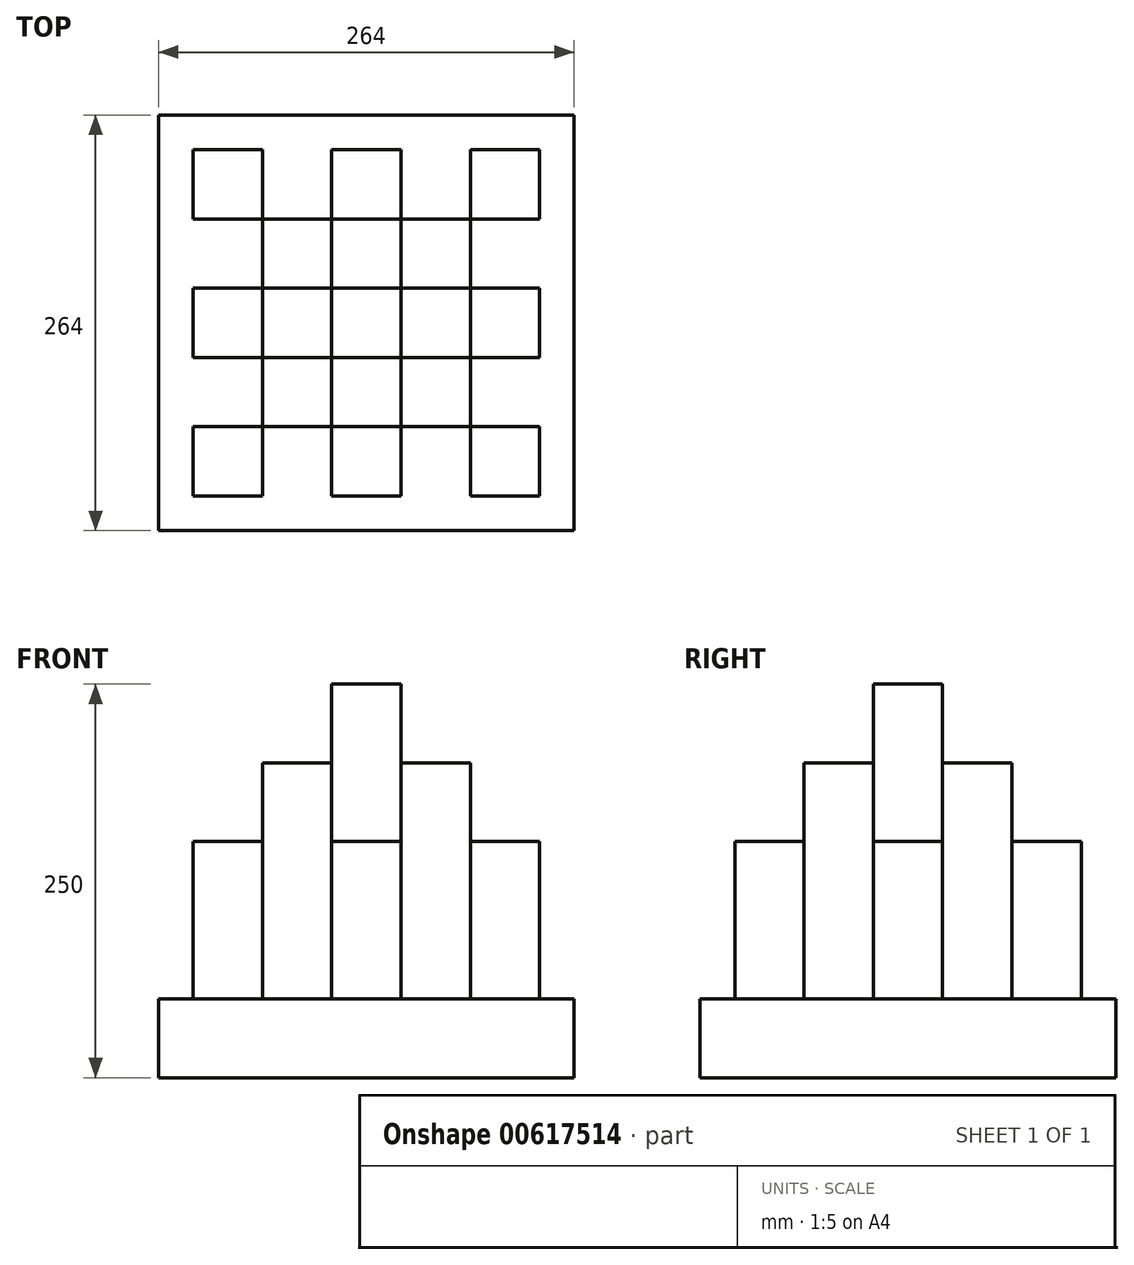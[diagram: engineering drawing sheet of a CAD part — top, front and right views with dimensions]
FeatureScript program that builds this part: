
annotation { "Feature Type Name" : "Feature", "Feature Type Description" : "" }
export const myFeature = defineFeature(function(context is Context, id is Id, definition is map)
    precondition{}
    {
        {
            var Q0;
            Q0=qCreatedBy(makeId("Top.planeOp"),FACE);
            var sketch = newSketch(context, id + "F0", { "sketchPlane" : qUnion([Q0])});
            skLineSegment(sketch, "E0.bottom", {"start": v(22, -22) * mm, "end": v(-22, -22) * mm});
            skLineSegment(sketch, "E0.top", {"start": v(22, 22) * mm, "end": v(-22, 22) * mm});
            skLineSegment(sketch, "E0.left", {"start": v(22, -22) * mm, "end": v(22, 22) * mm});
            skLineSegment(sketch, "E0.right", {"start": v(-22, -22) * mm, "end": v(-22, 22) * mm});
            skPoint(sketch, "E0.middle", {"position": v(0, 0) * mm});
            skLineSegment(sketch, "E1.bottom", {"start": v(-66, -22) * mm, "end": v(-110, -22) * mm});
            skLineSegment(sketch, "E1.top", {"start": v(-66, 22) * mm, "end": v(-110, 22) * mm});
            skLineSegment(sketch, "E1.left", {"start": v(-66, -22) * mm, "end": v(-66, 22) * mm});
            skLineSegment(sketch, "E1.right", {"start": v(-110, -22) * mm, "end": v(-110, 22) * mm});
            skPoint(sketch, "E1.middle", {"position": v(-88, 0) * mm});
            skPoint(sketch, "E1.middle.positionSnap0", {"position": v(-22, 0) * mm});
            skPoint(sketch, "E1.centerSnap0", {"position": v(-22, 0) * mm});
            skLineSegment(sketch, "E2.bottom", {"start": v(22, 66) * mm, "end": v(-22, 66) * mm});
            skLineSegment(sketch, "E2.top", {"start": v(22, 110) * mm, "end": v(-22, 110) * mm});
            skLineSegment(sketch, "E2.left", {"start": v(22, 66) * mm, "end": v(22, 110) * mm});
            skLineSegment(sketch, "E2.right", {"start": v(-22, 66) * mm, "end": v(-22, 110) * mm});
            skLineSegment(sketch, "E3.bottom", {"start": v(-66, 66) * mm, "end": v(-110, 66) * mm});
            skLineSegment(sketch, "E3.top", {"start": v(-66, 110) * mm, "end": v(-110, 110) * mm});
            skLineSegment(sketch, "E3.left", {"start": v(-66, 66) * mm, "end": v(-66, 110) * mm});
            skLineSegment(sketch, "E3.right", {"start": v(-110, 66) * mm, "end": v(-110, 110) * mm});
            skLineSegment(sketch, "E4.bottom", {"start": v(-132, 132) * mm, "end": v(132, 132) * mm});
            skLineSegment(sketch, "E4.top", {"start": v(-132, -132) * mm, "end": v(132, -132) * mm});
            skLineSegment(sketch, "E4.left", {"start": v(-132, 132) * mm, "end": v(-132, -132) * mm});
            skLineSegment(sketch, "E4.right", {"start": v(132, 132) * mm, "end": v(132, -132) * mm});
            skSolve(sketch);
        }
        {
            var Q0;
            Q0=makeQuery(id+"F0.imprint","IMPRINT",FACE,{"disambiguationData":[TD([[makeQuery(id+"F0.imprint","IMPRINT",EDGE,{"derivedFrom":sQuery(id+"F0.wireOp",EDGE,"E1.bottom")}),-1.0]])]});
            var Q1;
            Q1=makeQuery(id+"F0.imprint","IMPRINT",FACE,{"disambiguationData":[TD([[makeQuery(id+"F0.imprint","IMPRINT",EDGE,{"derivedFrom":sQuery(id+"F0.wireOp",EDGE,"E3.bottom")}),-1.0]])]});
            var Q2;
            Q2=makeQuery(id+"F0.imprint","IMPRINT",FACE,{"disambiguationData":[TD([[makeQuery(id+"F0.imprint","IMPRINT",EDGE,{"derivedFrom":sQuery(id+"F0.wireOp",EDGE,"E2.bottom")}),-1.0]])]});
            var Q3;
            Q3=makeQuery(id+"F0.imprint","IMPRINT",FACE,{"disambiguationData":[TD([[makeQuery(id+"F0.imprint","IMPRINT",EDGE,{"derivedFrom":sQuery(id+"F0.wireOp",EDGE,"E0.bottom")}),-1.0]])]});
            extrude(context, id + "F1", {"entities" : qUnion([Q0, Q1, Q2, Q3]), "depth" : 100 * mm, "offsetDistance" : 25 * mm});
        }
        {
            var Q0;
            Q0=makeQuery(id+"F1.opExtrude","SWEPT_BODY",BODY,{"disambiguationData":[OSD([sQuery(id+"F0.wireOp",EDGE,"E1.bottom"),sQuery(id+"F0.wireOp",EDGE,"E1.top"),sQuery(id+"F0.wireOp",EDGE,"E1.left"),sQuery(id+"F0.wireOp",EDGE,"E1.right")])]});
            var Q1;
            Q1=makeQuery(id+"F1.opExtrude","SWEPT_BODY",BODY,{"disambiguationData":[OSD([sQuery(id+"F0.wireOp",EDGE,"E3.bottom"),sQuery(id+"F0.wireOp",EDGE,"E3.top"),sQuery(id+"F0.wireOp",EDGE,"E3.left"),sQuery(id+"F0.wireOp",EDGE,"E3.right")])]});
            var Q2;
            Q2=qCreatedBy(makeId("Right.planeOp"),FACE);
            mirror(context, id + "F2", {"entities" : qUnion([Q0, Q1]), "mirrorPlane" : qUnion([Q2])});
        }
        {
            var Q0;
            Q0=makeQuery(id+"F1.opExtrude","SWEPT_BODY",BODY,{"disambiguationData":[OSD([sQuery(id+"F0.wireOp",EDGE,"E3.bottom"),sQuery(id+"F0.wireOp",EDGE,"E3.top"),sQuery(id+"F0.wireOp",EDGE,"E3.left"),sQuery(id+"F0.wireOp",EDGE,"E3.right")])]});
            var Q1;
            Q1=makeQuery(id+"F1.opExtrude","SWEPT_BODY",BODY,{"disambiguationData":[OSD([sQuery(id+"F0.wireOp",EDGE,"E2.bottom"),sQuery(id+"F0.wireOp",EDGE,"E2.top"),sQuery(id+"F0.wireOp",EDGE,"E2.left"),sQuery(id+"F0.wireOp",EDGE,"E2.right")])]});
            var Q2;
            Q2=makeQuery(id+"F2.opPattern","COPY",BODY,{"derivedFrom":makeQuery(id+"F1.opExtrude","SWEPT_BODY",BODY,{"disambiguationData":[OSD([sQuery(id+"F0.wireOp",EDGE,"E3.bottom"),sQuery(id+"F0.wireOp",EDGE,"E3.top"),sQuery(id+"F0.wireOp",EDGE,"E3.left"),sQuery(id+"F0.wireOp",EDGE,"E3.right")])]}),"instanceName":"1"});
            var Q3;
            Q3=qCreatedBy(makeId("Front.planeOp"),FACE);
            mirror(context, id + "F3", {"entities" : qUnion([Q0, Q1, Q2]), "mirrorPlane" : qUnion([Q3])});
        }
        {
            var Q0;
            Q0=makeQuery(id+"F0.imprint","IMPRINT",FACE,{"disambiguationData":[TD([[makeQuery(id+"F0.imprint","IMPRINT",EDGE,{"derivedFrom":sQuery(id+"F0.wireOp",EDGE,"E0.bottom")}),1.0]])]});
            var Q1;
            Q1=makeQuery(id+"F0.imprint","IMPRINT",FACE,{"disambiguationData":[TD([[makeQuery(id+"F0.imprint","IMPRINT",EDGE,{"derivedFrom":sQuery(id+"F0.wireOp",EDGE,"E1.bottom")}),-1.0]])]});
            var Q2;
            Q2=makeQuery(id+"F0.imprint","IMPRINT",FACE,{"disambiguationData":[TD([[makeQuery(id+"F0.imprint","IMPRINT",EDGE,{"derivedFrom":sQuery(id+"F0.wireOp",EDGE,"E0.bottom")}),-1.0]])]});
            var Q3;
            Q3=makeQuery(id+"F0.imprint","IMPRINT",FACE,{"disambiguationData":[TD([[makeQuery(id+"F0.imprint","IMPRINT",EDGE,{"derivedFrom":sQuery(id+"F0.wireOp",EDGE,"E3.bottom")}),-1.0]])]});
            var Q4;
            Q4=makeQuery(id+"F0.imprint","IMPRINT",FACE,{"disambiguationData":[TD([[makeQuery(id+"F0.imprint","IMPRINT",EDGE,{"derivedFrom":sQuery(id+"F0.wireOp",EDGE,"E2.bottom")}),-1.0]])]});
            var Q5;
            Q5=makeQuery(id+"F0.imprint","IMPRINT",FACE,{"disambiguationData":[TD([[makeQuery(id+"F0.imprint","IMPRINT",EDGE,{"derivedFrom":sQuery(id+"F0.wireOp",EDGE,"s8nrxy9o-eQNT-J21R-3rhY-hXZDEOxniQx1.bottom")}),-1.0]])]});
            var Q6;
            Q6=makeQuery(id+"F0.imprint","IMPRINT",FACE,{"disambiguationData":[TD([[makeQuery(id+"F0.imprint","IMPRINT",EDGE,{"derivedFrom":sQuery(id+"F0.wireOp",EDGE,"qjdVoqcM-cdFN-DcoX-eKo3-hN4eeX86174q.bottom")}),-1.0]])]});
            var Q7;
            Q7=makeQuery(id+"F0.imprint","IMPRINT",FACE,{"disambiguationData":[TD([[makeQuery(id+"F0.imprint","IMPRINT",EDGE,{"derivedFrom":sQuery(id+"F0.wireOp",EDGE,"QuOzhZ4j-HeuV-gT1i-nwIz-iXForqPxwVGl.bottom")}),-1.0]])]});
            var Q8;
            Q8=makeQuery(id+"F0.imprint","IMPRINT",FACE,{"disambiguationData":[TD([[makeQuery(id+"F0.imprint","IMPRINT",EDGE,{"derivedFrom":sQuery(id+"F0.wireOp",EDGE,"E0.top")}),-1.0]])]});
            var Q9;
            Q9=makeQuery(id+"F0.imprint","IMPRINT",FACE,{"disambiguationData":[TD([[makeQuery(id+"F0.imprint","IMPRINT",EDGE,{"derivedFrom":sQuery(id+"F0.wireOp",EDGE,"shoo1xml-Vqwe-dRvA-hi83-8JOpAzoyQhsb.bottom")}),-1.0]])]});
            var Q10;
            Q10=makeQuery(id+"F0.imprint","IMPRINT",FACE,{"disambiguationData":[TD([[makeQuery(id+"F0.imprint","IMPRINT",EDGE,{"derivedFrom":sQuery(id+"F0.wireOp",EDGE,"E0.right")}),1.0]])]});
            extrude(context, id + "F4", {"entities" : qUnion([Q0, Q1, Q2, Q3, Q4, Q5, Q6, Q7, Q8, Q9, Q10]), "oppositeDirection" : true, "depth" : 50 * mm, "offsetDistance" : 25 * mm});
        }
        {
            var Q0;
            Q0=makeQuery(id+"F4.opExtrude","CAP_FACE",FACE,{"disambiguationData":[OSD([sQuery(id+"F0.wireOp",EDGE,"E4.bottom"),sQuery(id+"F0.wireOp",EDGE,"E4.top"),sQuery(id+"F0.wireOp",EDGE,"E4.left"),sQuery(id+"F0.wireOp",EDGE,"E4.right")])],"isStart":true});
            var sketch = newSketch(context, id + "F5", { "sketchPlane" : qUnion([Q0])});
            skLineSegment(sketch, "E5.bottom", {"start": v(-66, 66) * mm, "end": v(-22, 66) * mm});
            skLineSegment(sketch, "E5.top", {"start": v(-66, 22) * mm, "end": v(-22, 22) * mm});
            skLineSegment(sketch, "E5.left", {"start": v(-66, 66) * mm, "end": v(-66, 22) * mm});
            skLineSegment(sketch, "E5.right", {"start": v(-22, 66) * mm, "end": v(-22, 22) * mm});
            skLineSegment(sketch, "E6.bottom", {"start": v(22, 66) * mm, "end": v(66, 66) * mm});
            skLineSegment(sketch, "E6.top", {"start": v(22, 22) * mm, "end": v(66, 22) * mm});
            skLineSegment(sketch, "E6.left", {"start": v(22, 66) * mm, "end": v(22, 22) * mm});
            skLineSegment(sketch, "E6.right", {"start": v(66, 66) * mm, "end": v(66, 22) * mm});
            skLineSegment(sketch, "E7.bottom", {"start": v(22, -22) * mm, "end": v(66, -22) * mm});
            skLineSegment(sketch, "E7.top", {"start": v(22, -66) * mm, "end": v(66, -66) * mm});
            skLineSegment(sketch, "E7.left", {"start": v(22, -22) * mm, "end": v(22, -66) * mm});
            skLineSegment(sketch, "E7.right", {"start": v(66, -22) * mm, "end": v(66, -66) * mm});
            skLineSegment(sketch, "E8.bottom", {"start": v(-66, -22) * mm, "end": v(-22, -22) * mm});
            skLineSegment(sketch, "E8.top", {"start": v(-66, -66) * mm, "end": v(-22, -66) * mm});
            skLineSegment(sketch, "E8.left", {"start": v(-66, -22) * mm, "end": v(-66, -66) * mm});
            skLineSegment(sketch, "E8.right", {"start": v(-22, -22) * mm, "end": v(-22, -66) * mm});
            skSolve(sketch);
        }
        {
            var Q0;
            Q0=makeQuery(id+"F5.imprint","IMPRINT",FACE,{"disambiguationData":[TD([[makeQuery(id+"F5.imprint","IMPRINT",EDGE,{"derivedFrom":sQuery(id+"F5.wireOp",EDGE,"E5.bottom")}),-1.0]])]});
            var Q1;
            Q1=makeQuery(id+"F5.imprint","IMPRINT",FACE,{"disambiguationData":[TD([[makeQuery(id+"F5.imprint","IMPRINT",EDGE,{"derivedFrom":sQuery(id+"F5.wireOp",EDGE,"E6.bottom")}),-1.0]])]});
            var Q2;
            Q2=makeQuery(id+"F5.imprint","IMPRINT",FACE,{"disambiguationData":[TD([[makeQuery(id+"F5.imprint","IMPRINT",EDGE,{"derivedFrom":sQuery(id+"F5.wireOp",EDGE,"E7.bottom")}),-1.0]])]});
            var Q3;
            Q3=makeQuery(id+"F5.imprint","IMPRINT",FACE,{"disambiguationData":[TD([[makeQuery(id+"F5.imprint","IMPRINT",EDGE,{"derivedFrom":sQuery(id+"F5.wireOp",EDGE,"E8.bottom")}),-1.0]])]});
            extrude(context, id + "F6", {"entities" : qUnion([Q0, Q1, Q2, Q3]), "depth" : 150 * mm, "offsetDistance" : 25 * mm});
        }
        {
            var Q0;
            Q0=makeQuery(id+"F1.opExtrude","CAP_FACE",FACE,{"disambiguationData":[OSD([sQuery(id+"F0.wireOp",EDGE,"E0.bottom"),sQuery(id+"F0.wireOp",EDGE,"E0.top"),sQuery(id+"F0.wireOp",EDGE,"E0.left"),sQuery(id+"F0.wireOp",EDGE,"E0.right")])],"isStart":false});
            extrude(context, id + "F7", {"entities" : qUnion([Q0]), "operationType" : NewBodyOperationType.ADD, "depth" : 100 * mm, "offsetDistance" : 25 * mm});
        }
    });
